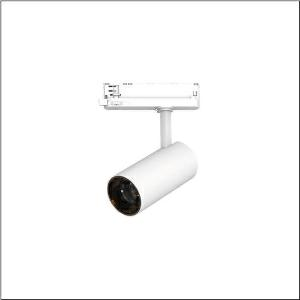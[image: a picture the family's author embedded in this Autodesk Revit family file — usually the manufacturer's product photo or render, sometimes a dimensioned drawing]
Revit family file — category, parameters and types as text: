
# Revit family: spot_31_slim_51sf137fb2b
name_source: partatom
category: Lighting Fixtures
units: mm (PartAtom-declared; Revit-internal decimal feet)

## family parameters
Cut with Voids When Loaded = No
Host = Face
Light Source = No
Part Type = Normal
Room Calculation Point = No
Round Connector Dimension = Use Diameter
Shared = No

## types (1)
- Spot 31 Slim (1 x LED, 2170 lm, 17.6 W, 3000K)
    Apparent Load = 18 VA
    CIE Flux Codes = 97 100 100 100 100
    Color Rendering = 90
    Color Temperature = 3000K
    Default Elevation = 1800 mm
    Description = Spot 31 Slim, directional spotlight, light control with reflector, of aluminium, LED rated luminous flux: 2.200lm, light colour: 930, control gear: ECG, with 3-phase adapter, mains connection: 220..240V, AC, 50/60Hz, housing, of aluminium, traffic white (RAL 9016), diameter: 70mm, adapter, of plastic, protection rating (complete): IP20, insulation class (complete): insulation class I (protective earthing), certification: CE, impact resistance: IK02, packaging unit: 1 piece
    Height = 210 mm
    Lamp = 1 x LED
    Lamp Light Flux = 2170 lm
    Lamp Power = 17.6 W
    Lamp count = 1
    Length = 70 mm
    Luminous efficacy = 123 lm/W
    Manufacturer = Siteco
    ModVariant = No
    Model = 51SF137FB2B
    Mounting Place = Ceiling
    Mounting Type = Pendant
    Number of Poles = 1
    OnlyDefault = Yes
    Power Factor = 1
    Product Name = Spot 31 Slim
    Product group = directional spotlight
    ProductGroupID = 905
    Protection Class = Protection class I
    Protection Degree = IP 20
    RLX_Detail_Level = 1
    RLX_Emergency_Light_Flux = 0 lm
    RLX_Emergency_Type = 0
    RLX_Emergency_Type_DB = No
    RlxData = <blob elided: 14145 chars, md5=d8b38c03>
    Socket = socket
    Standby Power = 0 W
    System Light Flux = 2170 lm
    System Power = 18 W
    Type Comments = Product without accessories
    Type Image = l_1228468.jpg
    URL = http://relux.com
    VarID = ---
    Voltage = 0 V
    Weight = 0.00 kg
    Width = 0 mm  [stored 0 ft]

note: [stored X ft] marks values corroborated as IEEE doubles in the binary element streams (Revit-internal decimal feet)

## geometry (parser evidence)
native form markers: Sweep x9
no freeform markers — native parametric forms only
